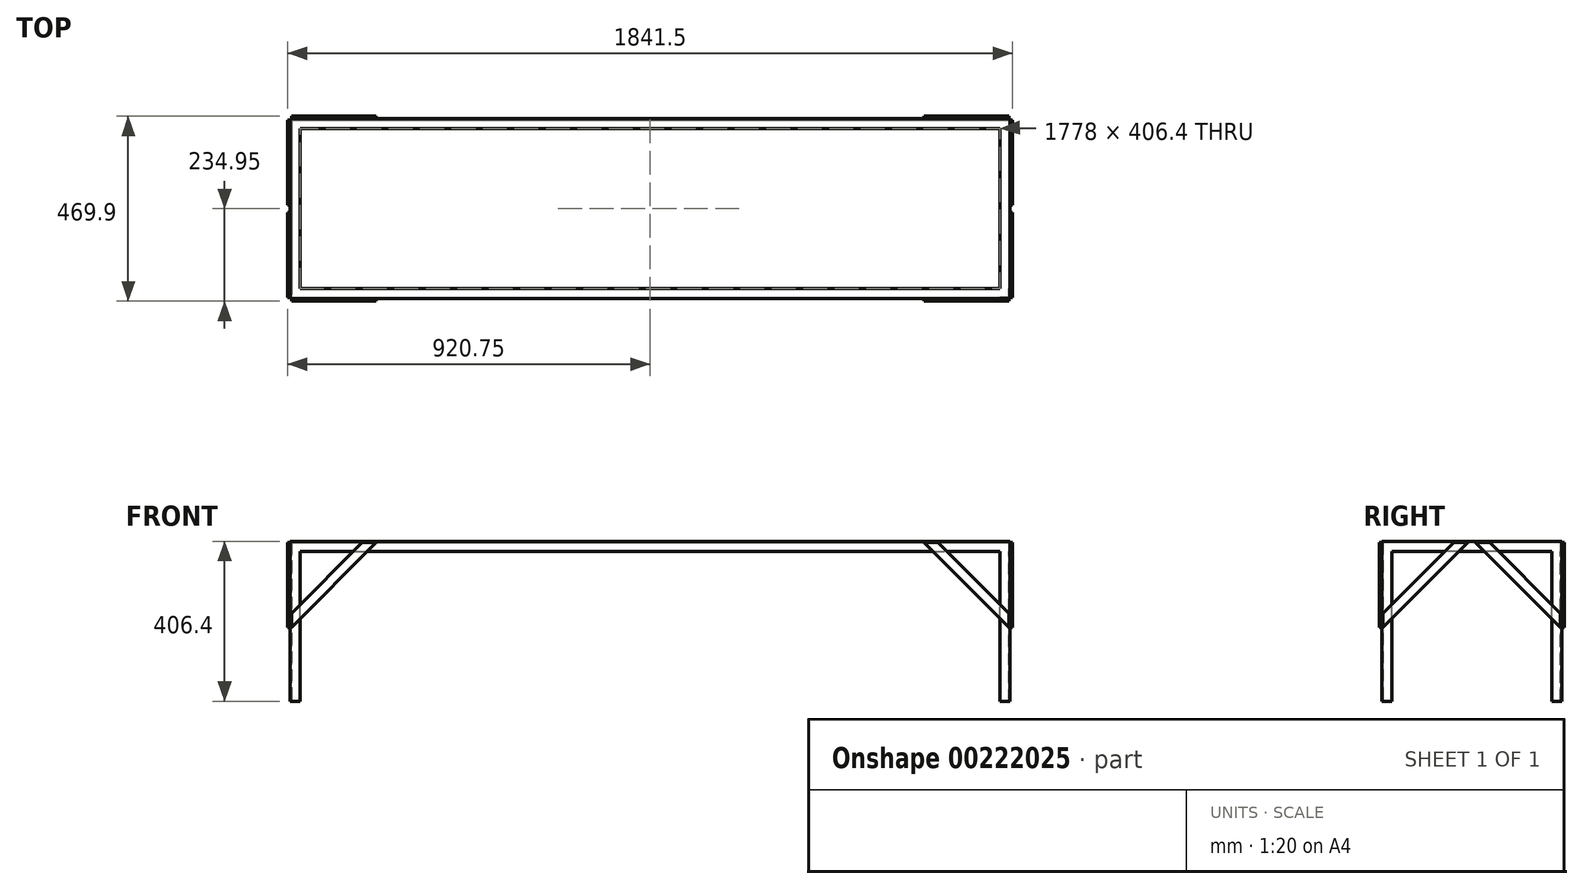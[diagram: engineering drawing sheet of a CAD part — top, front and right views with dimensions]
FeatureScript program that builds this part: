
annotation { "Feature Type Name" : "Feature", "Feature Type Description" : "" }
export const myFeature = defineFeature(function(context is Context, id is Id, definition is map)
    precondition{}
    {
        {
            var Q0;
            Q0=qCreatedBy(makeId("Top.planeOp"),FACE);
            var sketch = newSketch(context, id + "F0", { "sketchPlane" : qUnion([Q0])});
            skLineSegment(sketch, "E0.bottom", {"start": v(0, 0) * mm, "end": v(1828.8, 0) * mm});
            skLineSegment(sketch, "E0.top", {"start": v(0, -457.2) * mm, "end": v(1828.8, -457.2) * mm});
            skLineSegment(sketch, "E0.left", {"start": v(0, 0) * mm, "end": v(0, -457.2) * mm});
            skLineSegment(sketch, "E0.right", {"start": v(1828.8, 0) * mm, "end": v(1828.8, -457.2) * mm});
            skSolve(sketch);
        }
        {
            var Q0;
            Q0=makeQuery(id+"F0.imprint","IMPRINT",FACE,{"disambiguationData":[TD([[makeQuery(id+"F0.imprint","IMPRINT",EDGE,{"derivedFrom":sQuery(id+"F0.wireOp",EDGE,"E0.bottom")}),-1.0]])]});
            var sketch = newSketch(context, id + "F1", { "sketchPlane" : qUnion([Q0])});
            skLineSegment(sketch, "E1.0", {"start": v(25.4, -25.4) * mm, "end": v(1803.4, -25.4) * mm});
            skLineSegment(sketch, "E1.1", {"start": v(25.4, -25.4) * mm, "end": v(25.4, -431.8) * mm});
            skLineSegment(sketch, "E1.2", {"start": v(25.4, -431.8) * mm, "end": v(1803.4, -431.8) * mm});
            skLineSegment(sketch, "E1.3", {"start": v(1803.4, -25.4) * mm, "end": v(1803.4, -431.8) * mm});
            skSolve(sketch);
        }
        {
            var Q0;
            Q0=makeQuery(id+"F1.imprint","IMPRINT",FACE,{"disambiguationData":[TD([[makeQuery(id+"F1.imprint","IMPRINT",EDGE,{"derivedFrom":sQuery(id+"F1.wireOp",EDGE,"E1.0")}),1.0]])]});
            extrude(context, id + "F2", {"entities" : qUnion([Q0]), "depth" : 25.4 * mm});
        }
        {
            var Q0;
            Q0=makeQuery(id+"F2.opExtrude","SWEPT_FACE",FACE,{"disambiguationData":[OSD([sQuery(id+"F1.wireOp",EDGE,"E1.0")])]});
            var Q1;
            Q1=makeQuery(id+"F2.opExtrude","SWEPT_FACE",FACE,{"disambiguationData":[OSD([sQuery(id+"F1.wireOp",EDGE,"E1.3")])]});
            var Q2;
            Q2=makeQuery(id+"F2.opExtrude","SWEPT_FACE",FACE,{"disambiguationData":[OSD([sQuery(id+"F1.wireOp",EDGE,"E1.2")])]});
            var Q3;
            Q3=makeQuery(id+"F2.opExtrude","SWEPT_FACE",FACE,{"disambiguationData":[OSD([sQuery(id+"F1.wireOp",EDGE,"E1.1")])]});
            var Q4;
            Q4=makeQuery(id+"F2.opExtrude","CAP_FACE",FACE,{"disambiguationData":[OSD([sQuery(id+"F0.wireOp",EDGE,"E0.bottom"),sQuery(id+"F0.wireOp",EDGE,"E0.top"),sQuery(id+"F0.wireOp",EDGE,"E0.left"),sQuery(id+"F0.wireOp",EDGE,"E0.right"),sQuery(id+"F1.wireOp",EDGE,"E1.0"),sQuery(id+"F1.wireOp",EDGE,"E1.1"),sQuery(id+"F1.wireOp",EDGE,"E1.2"),sQuery(id+"F1.wireOp",EDGE,"E1.3")])],"isStart":true});
            shell(context, id + "F3", {"entities" : qUnion([Q0, Q1, Q2, Q3, Q4]), "thickness" : 3.17 * mm});
        }
        {
            var Q0;
            Q0=qCreatedBy(makeId("Top.planeOp"),FACE);
            var sketch = newSketch(context, id + "F4", { "sketchPlane" : qUnion([Q0])});
            skLineSegment(sketch, "E2.bottom", {"start": v(0, 0) * mm, "end": v(25.4, 0) * mm});
            skLineSegment(sketch, "E2.top", {"start": v(0, -25.4) * mm, "end": v(25.4, -25.4) * mm});
            skLineSegment(sketch, "E2.left", {"start": v(0, 0) * mm, "end": v(0, -25.4) * mm});
            skLineSegment(sketch, "E2.right", {"start": v(25.4, 0) * mm, "end": v(25.4, -25.4) * mm});
            skSolve(sketch);
        }
        {
            var Q0;
            Q0 = qSketchRegion(id + "F4", true);
            extrude(context, id + "F5", {"entities" : qUnion([Q0]), "oppositeDirection" : true, "depth" : 381 * mm});
        }
        {
            var Q0;
            Q0=makeQuery(id+"F5.opExtrude","SWEPT_FACE",FACE,{"disambiguationData":[OSD([sQuery(id+"F4.wireOp",EDGE,"E2.top")])]});
            var Q1;
            Q1=makeQuery(id+"F5.opExtrude","CAP_FACE",FACE,{"disambiguationData":[OSD([sQuery(id+"F4.wireOp",EDGE,"E2.bottom"),sQuery(id+"F4.wireOp",EDGE,"E2.top"),sQuery(id+"F4.wireOp",EDGE,"E2.left"),sQuery(id+"F4.wireOp",EDGE,"E2.right")])],"isStart":true});
            var Q2;
            Q2=makeQuery(id+"F5.opExtrude","CAP_FACE",FACE,{"disambiguationData":[OSD([sQuery(id+"F4.wireOp",EDGE,"E2.bottom"),sQuery(id+"F4.wireOp",EDGE,"E2.top"),sQuery(id+"F4.wireOp",EDGE,"E2.left"),sQuery(id+"F4.wireOp",EDGE,"E2.right")])],"isStart":false});
            var Q3;
            Q3=makeQuery(id+"F5.opExtrude","SWEPT_FACE",FACE,{"disambiguationData":[OSD([sQuery(id+"F4.wireOp",EDGE,"E2.right")])]});
            shell(context, id + "F6", {"entities" : qUnion([Q0, Q1, Q2, Q3]), "thickness" : 3.17 * mm});
        }
        {
            var Q0;
            Q0=makeQuery(id+"F5.opExtrude","SWEPT_BODY",BODY,{"disambiguationData":[OSD([sQuery(id+"F4.wireOp",EDGE,"E2.bottom"),sQuery(id+"F4.wireOp",EDGE,"E2.top"),sQuery(id+"F4.wireOp",EDGE,"E2.left"),sQuery(id+"F4.wireOp",EDGE,"E2.right")])]});
            var Q1;
            Q1=qCreatedBy(makeId("Front.planeOp"),FACE);
            transform(context, id + "F7", {"entities" : qUnion([Q0]), "transformType" : TransformType.TRANSLATION_DISTANCE, "transformDirection" : qUnion([Q1]), "distance" : 457.2 * mm, "makeCopy" : true});
        }
        {
            var Q0;
            Q0=makeQuery(id+"F7.opPattern","COPY",BODY,{"derivedFrom":makeQuery(id+"F5.opExtrude","SWEPT_BODY",BODY,{"disambiguationData":[OSD([sQuery(id+"F4.wireOp",EDGE,"E2.bottom"),sQuery(id+"F4.wireOp",EDGE,"E2.top"),sQuery(id+"F4.wireOp",EDGE,"E2.left"),sQuery(id+"F4.wireOp",EDGE,"E2.right")])]}),"instanceName":"1"});
            var Q1;
            Q1=makeQuery(id+"F7.opPattern","COPY",EDGE,{"derivedFrom":makeQuery(id+"F5.opExtrude","SWEPT_EDGE",EDGE,{"disambiguationData":[OSD([sQuery(id+"F4.wireOp",EDGE,"E2.bottom"),sQuery(id+"F4.wireOp",EDGE,"E2.left")])]}),"instanceName":"1"});
            transform(context, id + "F8", {"entities" : qUnion([Q0]), "transformType" : TransformType.ROTATION, "transformAxis" : qUnion([Q1]), "angle" : 90 * degree, "makeCopy" : false});
        }
        {
            var Q0;
            Q0=makeQuery(id+"F5.opExtrude","SWEPT_BODY",BODY,{"disambiguationData":[OSD([sQuery(id+"F4.wireOp",EDGE,"E2.bottom"),sQuery(id+"F4.wireOp",EDGE,"E2.top"),sQuery(id+"F4.wireOp",EDGE,"E2.left"),sQuery(id+"F4.wireOp",EDGE,"E2.right")])]});
            var Q1;
            Q1=makeQuery(id+"F7.opPattern","COPY",BODY,{"derivedFrom":makeQuery(id+"F5.opExtrude","SWEPT_BODY",BODY,{"disambiguationData":[OSD([sQuery(id+"F4.wireOp",EDGE,"E2.bottom"),sQuery(id+"F4.wireOp",EDGE,"E2.top"),sQuery(id+"F4.wireOp",EDGE,"E2.left"),sQuery(id+"F4.wireOp",EDGE,"E2.right")])]}),"instanceName":"1"});
            var Q2;
            Q2=sQuery(id+"F0.wireOp",EDGE,"E0.bottom");
            transform(context, id + "F9", {"entities" : qUnion([Q0, Q1]), "transformType" : TransformType.TRANSLATION_DISTANCE, "transformDirection" : qUnion([Q2]), "distance" : 1828.8 * mm, "makeCopy" : true});
        }
        {
            var Q0;
            Q0=makeQuery(id+"F9.opPattern","COPY",BODY,{"derivedFrom":makeQuery(id+"F5.opExtrude","SWEPT_BODY",BODY,{"disambiguationData":[OSD([sQuery(id+"F4.wireOp",EDGE,"E2.bottom"),sQuery(id+"F4.wireOp",EDGE,"E2.top"),sQuery(id+"F4.wireOp",EDGE,"E2.left"),sQuery(id+"F4.wireOp",EDGE,"E2.right")])]}),"instanceName":"1"});
            var Q1;
            Q1=makeQuery(id+"F9.opPattern","COPY",EDGE,{"derivedFrom":makeQuery(id+"F5.opExtrude","SWEPT_EDGE",EDGE,{"disambiguationData":[OSD([sQuery(id+"F4.wireOp",EDGE,"E2.bottom"),sQuery(id+"F4.wireOp",EDGE,"E2.left")])]}),"instanceName":"1"});
            transform(context, id + "F10", {"entities" : qUnion([Q0]), "transformType" : TransformType.ROTATION, "transformAxis" : qUnion([Q1]), "angle" : 90 * degree, "oppositeDirection" : true, "makeCopy" : false});
        }
        {
            var Q0;
            Q0=makeQuery(id+"F9.opPattern","COPY",BODY,{"derivedFrom":makeQuery(id+"F7.opPattern","COPY",BODY,{"derivedFrom":makeQuery(id+"F5.opExtrude","SWEPT_BODY",BODY,{"disambiguationData":[OSD([sQuery(id+"F4.wireOp",EDGE,"E2.bottom"),sQuery(id+"F4.wireOp",EDGE,"E2.top"),sQuery(id+"F4.wireOp",EDGE,"E2.left"),sQuery(id+"F4.wireOp",EDGE,"E2.right")])]}),"instanceName":"1"}),"instanceName":"1"});
            var Q1;
            Q1=makeQuery(id+"F9.opPattern","COPY",EDGE,{"derivedFrom":makeQuery(id+"F7.opPattern","COPY",EDGE,{"derivedFrom":makeQuery(id+"F5.opExtrude","SWEPT_EDGE",EDGE,{"disambiguationData":[OSD([sQuery(id+"F4.wireOp",EDGE,"E2.bottom"),sQuery(id+"F4.wireOp",EDGE,"E2.left")])]}),"instanceName":"1"}),"instanceName":"1"});
            transform(context, id + "F11", {"entities" : qUnion([Q0]), "transformType" : TransformType.ROTATION, "transformAxis" : qUnion([Q1]), "angle" : 90 * degree, "makeCopy" : false});
        }
        {
            var Q0;
            Q0=makeQuery(id+"F2.opExtrude","SWEPT_BODY",BODY,{"disambiguationData":[OSD([sQuery(id+"F0.wireOp",EDGE,"E0.bottom"),sQuery(id+"F0.wireOp",EDGE,"E0.top"),sQuery(id+"F0.wireOp",EDGE,"E0.left"),sQuery(id+"F0.wireOp",EDGE,"E0.right"),sQuery(id+"F1.wireOp",EDGE,"E1.0"),sQuery(id+"F1.wireOp",EDGE,"E1.1"),sQuery(id+"F1.wireOp",EDGE,"E1.2"),sQuery(id+"F1.wireOp",EDGE,"E1.3")])]});
            var Q1;
            Q1=makeQuery(id+"F5.opExtrude","SWEPT_BODY",BODY,{"disambiguationData":[OSD([sQuery(id+"F4.wireOp",EDGE,"E2.bottom"),sQuery(id+"F4.wireOp",EDGE,"E2.top"),sQuery(id+"F4.wireOp",EDGE,"E2.left"),sQuery(id+"F4.wireOp",EDGE,"E2.right")])]});
            var Q2;
            Q2=makeQuery(id+"F7.opPattern","COPY",BODY,{"derivedFrom":makeQuery(id+"F5.opExtrude","SWEPT_BODY",BODY,{"disambiguationData":[OSD([sQuery(id+"F4.wireOp",EDGE,"E2.bottom"),sQuery(id+"F4.wireOp",EDGE,"E2.top"),sQuery(id+"F4.wireOp",EDGE,"E2.left"),sQuery(id+"F4.wireOp",EDGE,"E2.right")])]}),"instanceName":"1"});
            var Q3;
            Q3=makeQuery(id+"F9.opPattern","COPY",BODY,{"derivedFrom":makeQuery(id+"F5.opExtrude","SWEPT_BODY",BODY,{"disambiguationData":[OSD([sQuery(id+"F4.wireOp",EDGE,"E2.bottom"),sQuery(id+"F4.wireOp",EDGE,"E2.top"),sQuery(id+"F4.wireOp",EDGE,"E2.left"),sQuery(id+"F4.wireOp",EDGE,"E2.right")])]}),"instanceName":"1"});
            var Q4;
            Q4=makeQuery(id+"F9.opPattern","COPY",BODY,{"derivedFrom":makeQuery(id+"F7.opPattern","COPY",BODY,{"derivedFrom":makeQuery(id+"F5.opExtrude","SWEPT_BODY",BODY,{"disambiguationData":[OSD([sQuery(id+"F4.wireOp",EDGE,"E2.bottom"),sQuery(id+"F4.wireOp",EDGE,"E2.top"),sQuery(id+"F4.wireOp",EDGE,"E2.left"),sQuery(id+"F4.wireOp",EDGE,"E2.right")])]}),"instanceName":"1"}),"instanceName":"1"});
            booleanBodies(context, id + "F12", {"operationType" : BooleanOperationType.UNION, "tools" : qUnion([Q0, Q1, Q2, Q3, Q4])});
        }
        {
            var Q0;
            Q0=qCreatedBy(makeId("Front.planeOp"),FACE);
            var sketch = newSketch(context, id + "F13", { "sketchPlane" : qUnion([Q0])});
            skLineSegment(sketch, "E3", {"start": v(0, 0) * mm, "end": v(-304.8, 0) * mm});
            skLineSegment(sketch, "E4", {"start": v(-304.8, 0) * mm, "end": v(-279.4, -25.4) * mm});
            skLineSegment(sketch, "E5", {"start": v(-279.4, -25.4) * mm, "end": v(-25.4, -25.4) * mm});
            skLineSegment(sketch, "E6", {"start": v(-25.4, -25.4) * mm, "end": v(0, 0) * mm});
            skSolve(sketch);
        }
        {
            var Q0;
            Q0 = qSketchRegion(id + "F13", true);
            extrude(context, id + "F14", {"entities" : qUnion([Q0]), "oppositeDirection" : true, "depth" : 6.35 * mm});
        }
        {
            var Q0;
            Q0=makeQuery(id+"F14.opExtrude","SWEPT_BODY",BODY,{"disambiguationData":[OSD([sQuery(id+"F13.wireOp",EDGE,"E3"),sQuery(id+"F13.wireOp",EDGE,"E4"),sQuery(id+"F13.wireOp",EDGE,"E5"),sQuery(id+"F13.wireOp",EDGE,"E6")])]});
            var Q1;
            Q1=makeQuery(id+"F2.opExtrude","CAP_EDGE",EDGE,{"disambiguationData":[OSD([sQuery(id+"F0.wireOp",EDGE,"E0.left")])],"isStart":true});
            transform(context, id + "F15", {"entities" : qUnion([Q0]), "transformType" : TransformType.ROTATION, "transformAxis" : qUnion([Q1]), "angle" : 225 * degree, "makeCopy" : false});
        }
        {
            var Q0;
            Q0=makeQuery(id+"F14.opExtrude","SWEPT_BODY",BODY,{"disambiguationData":[OSD([sQuery(id+"F13.wireOp",EDGE,"E3"),sQuery(id+"F13.wireOp",EDGE,"E4"),sQuery(id+"F13.wireOp",EDGE,"E5"),sQuery(id+"F13.wireOp",EDGE,"E6")])]});
            var Q1;
            Q1=makeQuery(id+"F12.opBoolean","MERGE",EDGE,{"derivedFrom":[makeQuery(id+"F2.opExtrude","SWEPT_EDGE",EDGE,{"disambiguationData":[OSD([sQuery(id+"F0.wireOp",EDGE,"E0.bottom"),sQuery(id+"F0.wireOp",EDGE,"E0.left")])]}),makeQuery(id+"F5.opExtrude","SWEPT_EDGE",EDGE,{"disambiguationData":[OSD([sQuery(id+"F4.wireOp",EDGE,"E2.bottom"),sQuery(id+"F4.wireOp",EDGE,"E2.left")])]})]});
            transform(context, id + "F16", {"entities" : qUnion([Q0]), "transformType" : TransformType.TRANSLATION_DISTANCE, "transformDirection" : qUnion([Q1]), "distance" : 193.54 * mm, "makeCopy" : false});
        }
        {
            var Q0;
            Q0=makeQuery(id+"F14.opExtrude","SWEPT_BODY",BODY,{"disambiguationData":[OSD([sQuery(id+"F13.wireOp",EDGE,"E3"),sQuery(id+"F13.wireOp",EDGE,"E4"),sQuery(id+"F13.wireOp",EDGE,"E5"),sQuery(id+"F13.wireOp",EDGE,"E6")])]});
            var Q1;
            Q1=makeQuery(id+"F2.opExtrude","CAP_EDGE",EDGE,{"disambiguationData":[OSD([sQuery(id+"F0.wireOp",EDGE,"E0.bottom")])],"isStart":false});
            transform(context, id + "F17", {"entities" : qUnion([Q0]), "transformType" : TransformType.TRANSLATION_DISTANCE, "transformDirection" : qUnion([Q1]), "distance" : 3.17 * mm, "makeCopy" : false});
        }
        {
            var Q0;
            Q0=makeQuery(id+"F14.opExtrude","SWEPT_BODY",BODY,{"disambiguationData":[OSD([sQuery(id+"F13.wireOp",EDGE,"E3"),sQuery(id+"F13.wireOp",EDGE,"E4"),sQuery(id+"F13.wireOp",EDGE,"E5"),sQuery(id+"F13.wireOp",EDGE,"E6")])]});
            var Q1;
            Q1=makeQuery(id+"F2.opExtrude","CAP_EDGE",EDGE,{"disambiguationData":[OSD([sQuery(id+"F0.wireOp",EDGE,"E0.right")])],"isStart":false});
            transform(context, id + "F18", {"entities" : qUnion([Q0]), "transformType" : TransformType.TRANSLATION_DISTANCE, "transformDirection" : qUnion([Q1]), "distance" : 463.55 * mm, "makeCopy" : true});
        }
        {
            var Q0;
            Q0=makeQuery(id+"F14.opExtrude","SWEPT_BODY",BODY,{"disambiguationData":[OSD([sQuery(id+"F13.wireOp",EDGE,"E3"),sQuery(id+"F13.wireOp",EDGE,"E4"),sQuery(id+"F13.wireOp",EDGE,"E5"),sQuery(id+"F13.wireOp",EDGE,"E6")])]});
            var Q1;
            Q1=makeQuery(id+"F12.opBoolean","MERGE",EDGE,{"derivedFrom":[makeQuery(id+"F2.opExtrude","SWEPT_EDGE",EDGE,{"disambiguationData":[OSD([sQuery(id+"F0.wireOp",EDGE,"E0.bottom"),sQuery(id+"F0.wireOp",EDGE,"E0.left")])]}),makeQuery(id+"F5.opExtrude","SWEPT_EDGE",EDGE,{"disambiguationData":[OSD([sQuery(id+"F4.wireOp",EDGE,"E2.bottom"),sQuery(id+"F4.wireOp",EDGE,"E2.left")])]})]});
            transform(context, id + "F19", {"entities" : qUnion([Q0]), "transformType" : TransformType.ROTATION, "transformAxis" : qUnion([Q1]), "angle" : 90 * degree, "makeCopy" : true});
        }
        {
            var Q0;
            Q0=makeQuery(id+"F18.opPattern","COPY",BODY,{"derivedFrom":makeQuery(id+"F14.opExtrude","SWEPT_BODY",BODY,{"disambiguationData":[OSD([sQuery(id+"F13.wireOp",EDGE,"E3"),sQuery(id+"F13.wireOp",EDGE,"E4"),sQuery(id+"F13.wireOp",EDGE,"E5"),sQuery(id+"F13.wireOp",EDGE,"E6")])]}),"instanceName":"1"});
            var Q1;
            Q1=makeQuery(id+"F12.opBoolean","MERGE",EDGE,{"derivedFrom":[makeQuery(id+"F2.opExtrude","SWEPT_EDGE",EDGE,{"disambiguationData":[OSD([sQuery(id+"F0.wireOp",EDGE,"E0.top"),sQuery(id+"F0.wireOp",EDGE,"E0.left")])]}),makeQuery(id+"F7.opPattern","COPY",EDGE,{"derivedFrom":makeQuery(id+"F5.opExtrude","SWEPT_EDGE",EDGE,{"disambiguationData":[OSD([sQuery(id+"F4.wireOp",EDGE,"E2.bottom"),sQuery(id+"F4.wireOp",EDGE,"E2.left")])]}),"instanceName":"1"})]});
            transform(context, id + "F20", {"entities" : qUnion([Q0]), "transformType" : TransformType.ROTATION, "transformAxis" : qUnion([Q1]), "angle" : 90 * degree, "oppositeDirection" : true, "makeCopy" : true});
        }
        {
            var Q0;
            Q0=makeQuery(id+"F19.opPattern","COPY",BODY,{"derivedFrom":makeQuery(id+"F14.opExtrude","SWEPT_BODY",BODY,{"disambiguationData":[OSD([sQuery(id+"F13.wireOp",EDGE,"E3"),sQuery(id+"F13.wireOp",EDGE,"E4"),sQuery(id+"F13.wireOp",EDGE,"E5"),sQuery(id+"F13.wireOp",EDGE,"E6")])]}),"instanceName":"1"});
            var Q1;
            Q1=makeQuery(id+"F20.opPattern","COPY",BODY,{"derivedFrom":makeQuery(id+"F18.opPattern","COPY",BODY,{"derivedFrom":makeQuery(id+"F14.opExtrude","SWEPT_BODY",BODY,{"disambiguationData":[OSD([sQuery(id+"F13.wireOp",EDGE,"E3"),sQuery(id+"F13.wireOp",EDGE,"E4"),sQuery(id+"F13.wireOp",EDGE,"E5"),sQuery(id+"F13.wireOp",EDGE,"E6")])]}),"instanceName":"1"}),"instanceName":"1"});
            var Q2;
            Q2=makeQuery(id+"F2.opExtrude","CAP_EDGE",EDGE,{"disambiguationData":[OSD([sQuery(id+"F0.wireOp",EDGE,"E0.top")])],"isStart":false});
            transform(context, id + "F21", {"entities" : qUnion([Q0, Q1]), "transformType" : TransformType.TRANSLATION_DISTANCE, "transformDirection" : qUnion([Q2]), "distance" : 6.35 * mm, "oppositeDirection" : true, "makeCopy" : false});
        }
        {
            var Q0;
            Q0=makeQuery(id+"F19.opPattern","COPY",BODY,{"derivedFrom":makeQuery(id+"F14.opExtrude","SWEPT_BODY",BODY,{"disambiguationData":[OSD([sQuery(id+"F13.wireOp",EDGE,"E3"),sQuery(id+"F13.wireOp",EDGE,"E4"),sQuery(id+"F13.wireOp",EDGE,"E5"),sQuery(id+"F13.wireOp",EDGE,"E6")])]}),"instanceName":"1"});
            var Q1;
            Q1=makeQuery(id+"F20.opPattern","COPY",BODY,{"derivedFrom":makeQuery(id+"F18.opPattern","COPY",BODY,{"derivedFrom":makeQuery(id+"F14.opExtrude","SWEPT_BODY",BODY,{"disambiguationData":[OSD([sQuery(id+"F13.wireOp",EDGE,"E3"),sQuery(id+"F13.wireOp",EDGE,"E4"),sQuery(id+"F13.wireOp",EDGE,"E5"),sQuery(id+"F13.wireOp",EDGE,"E6")])]}),"instanceName":"1"}),"instanceName":"1"});
            var Q2;
            Q2=makeQuery(id+"F2.opExtrude","CAP_EDGE",EDGE,{"disambiguationData":[OSD([sQuery(id+"F0.wireOp",EDGE,"E0.top")])],"isStart":false});
            transform(context, id + "F22", {"entities" : qUnion([Q0, Q1]), "transformType" : TransformType.TRANSLATION_DISTANCE, "transformDirection" : qUnion([Q2]), "distance" : 1835.15 * mm, "makeCopy" : true});
        }
        {
            var Q0;
            Q0=makeQuery(id+"F22.opPattern","COPY",BODY,{"derivedFrom":makeQuery(id+"F20.opPattern","COPY",BODY,{"derivedFrom":makeQuery(id+"F18.opPattern","COPY",BODY,{"derivedFrom":makeQuery(id+"F14.opExtrude","SWEPT_BODY",BODY,{"disambiguationData":[OSD([sQuery(id+"F13.wireOp",EDGE,"E3"),sQuery(id+"F13.wireOp",EDGE,"E4"),sQuery(id+"F13.wireOp",EDGE,"E5"),sQuery(id+"F13.wireOp",EDGE,"E6")])]}),"instanceName":"1"}),"instanceName":"1"}),"instanceName":"1"});
            var Q1;
            Q1=makeQuery(id+"F12.opBoolean","MERGE",EDGE,{"derivedFrom":[makeQuery(id+"F2.opExtrude","SWEPT_EDGE",EDGE,{"disambiguationData":[OSD([sQuery(id+"F0.wireOp",EDGE,"E0.top"),sQuery(id+"F0.wireOp",EDGE,"E0.right")])]}),makeQuery(id+"F9.opPattern","COPY",EDGE,{"derivedFrom":makeQuery(id+"F7.opPattern","COPY",EDGE,{"derivedFrom":makeQuery(id+"F5.opExtrude","SWEPT_EDGE",EDGE,{"disambiguationData":[OSD([sQuery(id+"F4.wireOp",EDGE,"E2.bottom"),sQuery(id+"F4.wireOp",EDGE,"E2.left")])]}),"instanceName":"1"}),"instanceName":"1"})]});
            transform(context, id + "F23", {"entities" : qUnion([Q0]), "transformType" : TransformType.ROTATION, "transformAxis" : qUnion([Q1]), "angle" : 90 * degree, "oppositeDirection" : true, "makeCopy" : true});
        }
        {
            var Q0;
            Q0=makeQuery(id+"F22.opPattern","COPY",BODY,{"derivedFrom":makeQuery(id+"F19.opPattern","COPY",BODY,{"derivedFrom":makeQuery(id+"F14.opExtrude","SWEPT_BODY",BODY,{"disambiguationData":[OSD([sQuery(id+"F13.wireOp",EDGE,"E3"),sQuery(id+"F13.wireOp",EDGE,"E4"),sQuery(id+"F13.wireOp",EDGE,"E5"),sQuery(id+"F13.wireOp",EDGE,"E6")])]}),"instanceName":"1"}),"instanceName":"1"});
            var Q1;
            Q1=makeQuery(id+"F12.opBoolean","MERGE",EDGE,{"derivedFrom":[makeQuery(id+"F3.opShell","OFFSET_EDGE",EDGE,{"disambiguationData":[OSD([sQuery(id+"F0.wireOp",EDGE,"E0.bottom"),sQuery(id+"F0.wireOp",EDGE,"E0.right")])]}),makeQuery(id+"F9.opPattern","COPY",EDGE,{"derivedFrom":makeQuery(id+"F6.opShell","OFFSET_EDGE",EDGE,{"disambiguationData":[OSD([sQuery(id+"F4.wireOp",EDGE,"E2.bottom"),sQuery(id+"F4.wireOp",EDGE,"E2.left")])]}),"instanceName":"1"})]});
            transform(context, id + "F24", {"entities" : qUnion([Q0]), "transformType" : TransformType.ROTATION, "transformAxis" : qUnion([Q1]), "angle" : 90 * degree, "makeCopy" : true});
        }
        {
            var Q0;
            Q0=makeQuery(id+"F23.opPattern","COPY",BODY,{"derivedFrom":makeQuery(id+"F22.opPattern","COPY",BODY,{"derivedFrom":makeQuery(id+"F20.opPattern","COPY",BODY,{"derivedFrom":makeQuery(id+"F18.opPattern","COPY",BODY,{"derivedFrom":makeQuery(id+"F14.opExtrude","SWEPT_BODY",BODY,{"disambiguationData":[OSD([sQuery(id+"F13.wireOp",EDGE,"E3"),sQuery(id+"F13.wireOp",EDGE,"E4"),sQuery(id+"F13.wireOp",EDGE,"E5"),sQuery(id+"F13.wireOp",EDGE,"E6")])]}),"instanceName":"1"}),"instanceName":"1"}),"instanceName":"1"}),"instanceName":"1"});
            var Q1;
            {var subQ0=sQuery(id+"F0.wireOp",EDGE,"E0.right");Q1=makeQuery(id+"F3.opShell","OFFSET_EDGE",EDGE,{"disambiguationData":[OSD([subQ0]),TDD([makeQuery(id+"F2.opExtrude","CAP_EDGE",EDGE,{"disambiguationData":[OSD([subQ0])],"isStart":false})])]});}
            transform(context, id + "F25", {"entities" : qUnion([Q0]), "transformType" : TransformType.TRANSLATION_DISTANCE, "transformDirection" : qUnion([Q1]), "distance" : 6.35 * mm, "makeCopy" : false});
        }
        {
            var Q0;
            Q0=makeQuery(id+"F24.opPattern","COPY",BODY,{"derivedFrom":makeQuery(id+"F22.opPattern","COPY",BODY,{"derivedFrom":makeQuery(id+"F19.opPattern","COPY",BODY,{"derivedFrom":makeQuery(id+"F14.opExtrude","SWEPT_BODY",BODY,{"disambiguationData":[OSD([sQuery(id+"F13.wireOp",EDGE,"E3"),sQuery(id+"F13.wireOp",EDGE,"E4"),sQuery(id+"F13.wireOp",EDGE,"E5"),sQuery(id+"F13.wireOp",EDGE,"E6")])]}),"instanceName":"1"}),"instanceName":"1"}),"instanceName":"1"});
            var Q1;
            {var subQ0=sQuery(id+"F0.wireOp",EDGE,"E0.right");Q1=makeQuery(id+"F3.opShell","OFFSET_EDGE",EDGE,{"disambiguationData":[OSD([subQ0]),TDD([makeQuery(id+"F2.opExtrude","CAP_EDGE",EDGE,{"disambiguationData":[OSD([subQ0])],"isStart":false})])]});}
            transform(context, id + "F26", {"entities" : qUnion([Q0]), "transformType" : TransformType.TRANSLATION_DISTANCE, "transformDirection" : qUnion([Q1]), "distance" : 12.7 * mm, "oppositeDirection" : true, "makeCopy" : false});
        }
    });
